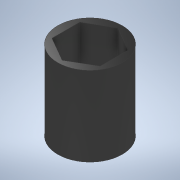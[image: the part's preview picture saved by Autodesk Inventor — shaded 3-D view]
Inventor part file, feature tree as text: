
AUTODESK INVENTOR PART (.ipt)
format: ipt  version: 2020 (Build 240168000, 168)  size: 103,424 bytes
history: native  units: in
note: dims shown in document units (in); Inventor stores cm internally (conversion verified against a paired STEP export)
features: extrude x1, sketch x1
ambient origin geometry x8: Origin, YZ Plane, XZ Plane, XY Plane, X Axis, Y Axis, Z Axis, Center Point
bodies: Solid1 (feature_tree)
feature tree (2):
  extrude  "Extrusion1"  Depth=0.617in
  sketch  "Sketch1"  dims[d0=0.375in d1=0.5in d2=0.617in d3=0.0in]
